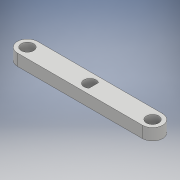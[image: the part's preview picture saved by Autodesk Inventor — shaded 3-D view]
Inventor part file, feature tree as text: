
AUTODESK INVENTOR PART (.ipt)
format: ipt  version: 2018 (Build 220112000, 112)  size: 110,080 bytes
history: native  units: mm
features: extrude x1, sketch x1
ambient origin geometry x8: Origin, YZ Plane, XZ Plane, XY Plane, X Axis, Y Axis, Z Axis, Center Point
bodies: Solid1 (feature_tree)
feature tree (2):
  extrude  "Extrusion1"  Depth=3.0mm
  sketch  "Sketch1"  dims[d0=3.15mm d1=3.2mm d2=3.2mm d3=16.2mm d4=16.2mm d5=5.2mm d6=5.2mm d7=3.0mm d8=0.0mm d9=2.55mm]
